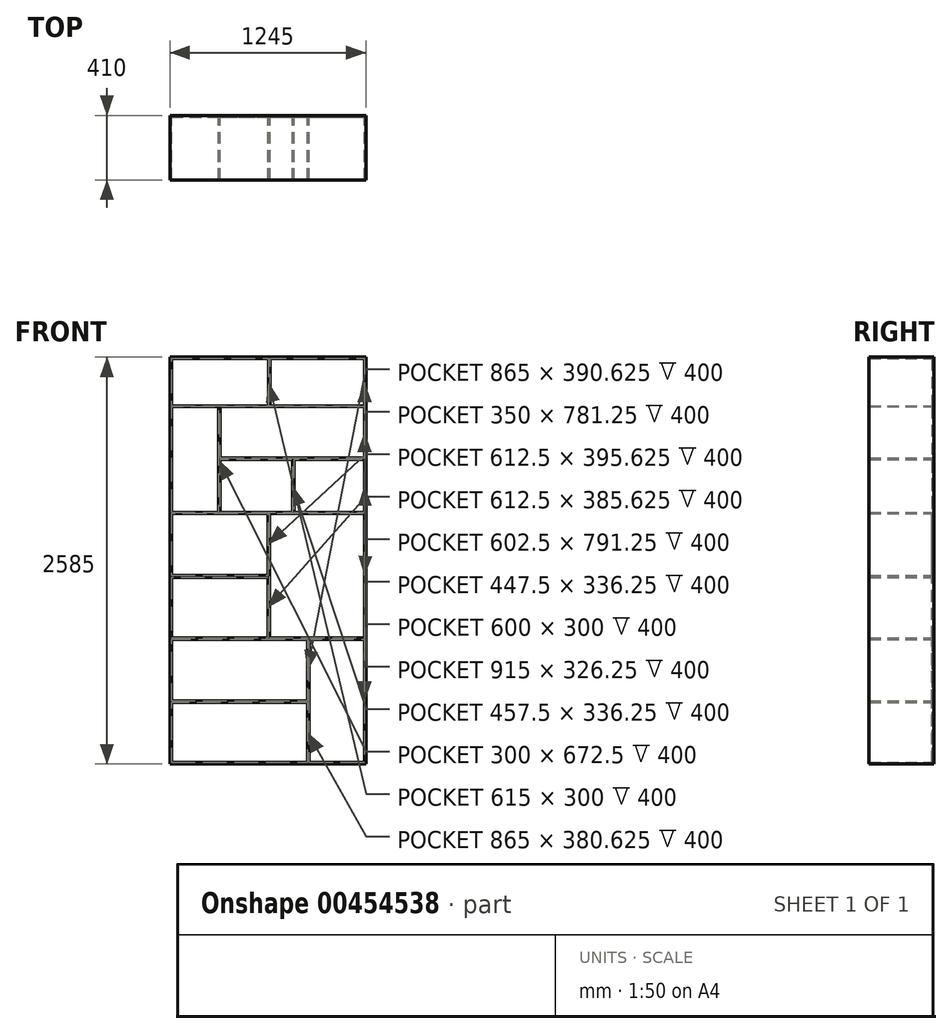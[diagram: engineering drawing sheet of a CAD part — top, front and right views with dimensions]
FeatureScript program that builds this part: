
annotation { "Feature Type Name" : "Feature", "Feature Type Description" : "" }
export const myFeature = defineFeature(function(context is Context, id is Id, definition is map)
    precondition{}
    {
        {
            var Q0;
            Q0=qCreatedBy(makeId("Front.planeOp"),FACE);
            var sketch = newSketch(context, id + "F0", { "sketchPlane" : qUnion([Q0])});
            skLineSegment(sketch, "E0.bottom", {"start": v(0, 0) * mm, "end": v(1245, 0) * mm});
            skLineSegment(sketch, "E0.top", {"start": v(0, 2585) * mm, "end": v(1245, 2585) * mm});
            skLineSegment(sketch, "E0.left", {"start": v(0, 0) * mm, "end": v(0, 2585) * mm});
            skLineSegment(sketch, "E0.right", {"start": v(1245, 0) * mm, "end": v(1245, 2585) * mm});
            skSolve(sketch);
        }
        {
            var Q0;
            Q0 = qSketchRegion(id + "F0", true);
            extrude(context, id + "F1", {"entities" : qUnion([Q0]), "depth" : 410 * mm});
        }
        {
            var Q0;
            Q0=makeQuery(id+"F1.opExtrude","CAP_FACE",FACE,{"disambiguationData":[OSD([sQuery(id+"F0.wireOp",EDGE,"E0.bottom"),sQuery(id+"F0.wireOp",EDGE,"E0.top"),sQuery(id+"F0.wireOp",EDGE,"E0.left"),sQuery(id+"F0.wireOp",EDGE,"E0.right")])],"isStart":false});
            shell(context, id + "F2", {"entities" : qUnion([Q0]), "thickness" : 10 * mm});
        }
        {
            var Q0;
            Q0=makeQuery(id+"F2.opShell","OFFSET_FACE",FACE,{"disambiguationData":[OSD([sQuery(id+"F0.wireOp",EDGE,"E0.bottom"),sQuery(id+"F0.wireOp",EDGE,"E0.top"),sQuery(id+"F0.wireOp",EDGE,"E0.left"),sQuery(id+"F0.wireOp",EDGE,"E0.right")])]});
            var sketch = newSketch(context, id + "F3", { "sketchPlane" : qUnion([Q0])});
            skLineSegment(sketch, "E1", {"start": v(622.5, 2575) * mm, "end": v(622.5, 10) * mm, "construction": true});
            skLineSegment(sketch, "E2", {"start": v(10, 1292.5) * mm, "end": v(1235, 1292.5) * mm, "construction": true});
            skLineSegment(sketch, "E3", {"start": v(1235, 1292.5) * mm, "end": v(1235, 1592.5) * mm, "construction": true});
            skLineSegment(sketch, "E4", {"start": v(1235, 1592.5) * mm, "end": v(10, 1592.5) * mm, "construction": true});
            skLineSegment(sketch, "E5", {"start": v(10, 992.5) * mm, "end": v(1235, 992.5) * mm, "construction": true});
            skLineSegment(sketch, "E6", {"start": v(10, 2270) * mm, "end": v(1235, 2270) * mm, "construction": true});
            skLineSegment(sketch, "E7", {"start": v(10, 610) * mm, "end": v(1235, 610) * mm, "construction": true});
            skLineSegment(sketch, "E8.bottom", {"start": v(10, 2270) * mm, "end": v(1235, 2270) * mm});
            skLineSegment(sketch, "E8.top", {"start": v(10, 2275) * mm, "end": v(1235, 2275) * mm});
            skLineSegment(sketch, "E8.left", {"start": v(10, 2270) * mm, "end": v(10, 2275) * mm});
            skLineSegment(sketch, "E8.right", {"start": v(1235, 2270) * mm, "end": v(1235, 2275) * mm});
            skLineSegment(sketch, "E9", {"start": v(10, 1592.5) * mm, "end": v(1235, 1592.5) * mm, "construction": true});
            skLineSegment(sketch, "E10.bottom", {"start": v(10, 1592.5) * mm, "end": v(1235, 1592.5) * mm});
            skLineSegment(sketch, "E10.top", {"start": v(10, 1597.5) * mm, "end": v(1235, 1597.5) * mm});
            skLineSegment(sketch, "E10.left", {"start": v(10, 1592.5) * mm, "end": v(10, 1597.5) * mm});
            skLineSegment(sketch, "E10.right", {"start": v(1235, 1592.5) * mm, "end": v(1235, 1597.5) * mm});
            skSolve(sketch);
        }
        {
            var Q0;
            Q0 = qSketchRegion(id + "F3", true);
            extrude(context, id + "F4", {"entities" : qUnion([Q0]), "operationType" : NewBodyOperationType.ADD, "depth" : 400 * mm});
        }
        {
            var Q0;
            {var subQ0=sQuery(id+"F0.wireOp",EDGE,"E0.left");var subQ1=sQuery(id+"F0.wireOp",EDGE,"E0.right");Q0=makeQuery(id+"F4.boolean.opBoolean","SPLIT",FACE,{"disambiguationData":[TD([makeQuery(id+"F4.opExtrude","SWEPT_FACE",FACE,{"disambiguationData":[OSD([sQuery(id+"F3.wireOp",EDGE,"E8.bottom")])]})])],"derivedFrom":makeQuery(id+"F2.opShell","OFFSET_FACE",FACE,{"disambiguationData":[OSD([sQuery(id+"F0.wireOp",EDGE,"E0.bottom"),sQuery(id+"F0.wireOp",EDGE,"E0.top"),subQ0,subQ1])]})});}
            var sketch = newSketch(context, id + "F5", { "sketchPlane" : qUnion([Q0])});
            skLineSegment(sketch, "E11.bottom", {"start": v(310, 2270) * mm, "end": v(320, 2270) * mm});
            skLineSegment(sketch, "E11.top", {"start": v(310, 1597.5) * mm, "end": v(320, 1597.5) * mm});
            skLineSegment(sketch, "E11.left", {"start": v(310, 2270) * mm, "end": v(310, 1597.5) * mm});
            skLineSegment(sketch, "E11.right", {"start": v(320, 2270) * mm, "end": v(320, 1597.5) * mm});
            skSolve(sketch);
        }
        {
            var Q0;
            Q0 = qSketchRegion(id + "F5", true);
            extrude(context, id + "F6", {"entities" : qUnion([Q0]), "operationType" : NewBodyOperationType.ADD, "depth" : 400 * mm});
        }
        {
            var Q0;
            {var subQ0=sQuery(id+"F0.wireOp",EDGE,"E0.right");var subQ1=makeQuery(id+"F2.opShell","OFFSET_FACE",FACE,{"disambiguationData":[OSD([subQ0])]});var subQ2=makeQuery(id+"F4.opExtrude","SWEPT_FACE",FACE,{"disambiguationData":[OSD([sQuery(id+"F3.wireOp",EDGE,"E8.bottom")])]});var subQ4=sQuery(id+"F0.wireOp",EDGE,"E0.left");Q0=makeQuery(id+"F6.boolean.opBoolean","SPLIT",FACE,{"disambiguationData":[TD([subQ1])],"derivedFrom":makeQuery(id+"F4.boolean.opBoolean","SPLIT",FACE,{"disambiguationData":[TD([subQ2])],"derivedFrom":makeQuery(id+"F2.opShell","OFFSET_FACE",FACE,{"disambiguationData":[OSD([sQuery(id+"F0.wireOp",EDGE,"E0.bottom"),sQuery(id+"F0.wireOp",EDGE,"E0.top"),subQ4,subQ0])]})})});}
            var sketch = newSketch(context, id + "F7", { "sketchPlane" : qUnion([Q0])});
            skLineSegment(sketch, "E12.bottom", {"start": v(320, 1943.75) * mm, "end": v(1235, 1943.75) * mm});
            skLineSegment(sketch, "E12.top", {"start": v(320, 1933.75) * mm, "end": v(1235, 1933.75) * mm});
            skLineSegment(sketch, "E12.left", {"start": v(320, 1943.75) * mm, "end": v(320, 1933.75) * mm});
            skLineSegment(sketch, "E12.right", {"start": v(1235, 1943.75) * mm, "end": v(1235, 1933.75) * mm});
            skSolve(sketch);
        }
        {
            var Q0;
            Q0 = qSketchRegion(id + "F7", true);
            extrude(context, id + "F8", {"entities" : qUnion([Q0]), "operationType" : NewBodyOperationType.ADD, "depth" : 400 * mm});
        }
        {
            var Q0;
            {var subQ0=sQuery(id+"F0.wireOp",EDGE,"E0.top");var subQ1=sQuery(id+"F0.wireOp",EDGE,"E0.left");var subQ2=sQuery(id+"F0.wireOp",EDGE,"E0.right");Q0=makeQuery(id+"F4.boolean.opBoolean","SPLIT",FACE,{"disambiguationData":[TD([makeQuery(id+"F2.opShell","OFFSET_FACE",FACE,{"disambiguationData":[OSD([subQ0])]})])],"derivedFrom":makeQuery(id+"F2.opShell","OFFSET_FACE",FACE,{"disambiguationData":[OSD([sQuery(id+"F0.wireOp",EDGE,"E0.bottom"),subQ0,subQ1,subQ2])]})});}
            var sketch = newSketch(context, id + "F9", { "sketchPlane" : qUnion([Q0])});
            skLineSegment(sketch, "E13.bottom", {"start": v(625, 2575) * mm, "end": v(635, 2575) * mm});
            skLineSegment(sketch, "E13.top", {"start": v(625, 2275) * mm, "end": v(635, 2275) * mm});
            skLineSegment(sketch, "E13.left", {"start": v(625, 2575) * mm, "end": v(625, 2275) * mm});
            skLineSegment(sketch, "E13.right", {"start": v(635, 2575) * mm, "end": v(635, 2275) * mm});
            skSolve(sketch);
        }
        {
            var Q0;
            Q0 = qSketchRegion(id + "F9", true);
            extrude(context, id + "F10", {"entities" : qUnion([Q0]), "operationType" : NewBodyOperationType.ADD, "depth" : 400 * mm});
        }
        {
            var Q0;
            {var subQ0=sQuery(id+"F0.wireOp",EDGE,"E0.right");var subQ1=makeQuery(id+"F2.opShell","OFFSET_FACE",FACE,{"disambiguationData":[OSD([subQ0])]});var subQ2=makeQuery(id+"F4.opExtrude","SWEPT_FACE",FACE,{"disambiguationData":[OSD([sQuery(id+"F3.wireOp",EDGE,"E10.top")])]});var subQ4=makeQuery(id+"F4.opExtrude","SWEPT_FACE",FACE,{"disambiguationData":[OSD([sQuery(id+"F3.wireOp",EDGE,"E8.bottom")])]});var subQ5=sQuery(id+"F0.wireOp",EDGE,"E0.left");Q0=makeQuery(id+"F8.boolean.opBoolean","SPLIT",FACE,{"disambiguationData":[TD([subQ2])],"derivedFrom":makeQuery(id+"F6.boolean.opBoolean","SPLIT",FACE,{"disambiguationData":[TD([subQ1])],"derivedFrom":makeQuery(id+"F4.boolean.opBoolean","SPLIT",FACE,{"disambiguationData":[TD([subQ4])],"derivedFrom":makeQuery(id+"F2.opShell","OFFSET_FACE",FACE,{"disambiguationData":[OSD([sQuery(id+"F0.wireOp",EDGE,"E0.bottom"),sQuery(id+"F0.wireOp",EDGE,"E0.top"),subQ5,subQ0])]})})})});}
            var sketch = newSketch(context, id + "F11", { "sketchPlane" : qUnion([Q0])});
            skLineSegment(sketch, "E14.bottom", {"start": v(777.5, 1933.75) * mm, "end": v(787.5, 1933.75) * mm});
            skLineSegment(sketch, "E14.top", {"start": v(777.5, 1597.5) * mm, "end": v(787.5, 1597.5) * mm});
            skLineSegment(sketch, "E14.left", {"start": v(777.5, 1933.75) * mm, "end": v(777.5, 1597.5) * mm});
            skLineSegment(sketch, "E14.right", {"start": v(787.5, 1933.75) * mm, "end": v(787.5, 1597.5) * mm});
            skSolve(sketch);
        }
        {
            var Q0;
            Q0 = qSketchRegion(id + "F11", true);
            extrude(context, id + "F12", {"entities" : qUnion([Q0]), "operationType" : NewBodyOperationType.ADD, "depth" : 400 * mm});
        }
        {
            var Q0;
            {var subQ0=sQuery(id+"F0.wireOp",EDGE,"E0.bottom");var subQ1=sQuery(id+"F0.wireOp",EDGE,"E0.left");var subQ2=sQuery(id+"F0.wireOp",EDGE,"E0.right");Q0=makeQuery(id+"F4.boolean.opBoolean","SPLIT",FACE,{"disambiguationData":[TD([makeQuery(id+"F2.opShell","OFFSET_FACE",FACE,{"disambiguationData":[OSD([subQ0])]})])],"derivedFrom":makeQuery(id+"F2.opShell","OFFSET_FACE",FACE,{"disambiguationData":[OSD([subQ0,sQuery(id+"F0.wireOp",EDGE,"E0.top"),subQ1,subQ2])]})});}
            var sketch = newSketch(context, id + "F13", { "sketchPlane" : qUnion([Q0])});
            skLineSegment(sketch, "E15.bottom", {"start": v(10, 801.25) * mm, "end": v(1235, 801.25) * mm});
            skLineSegment(sketch, "E15.top", {"start": v(10, 791.25) * mm, "end": v(1235, 791.25) * mm});
            skLineSegment(sketch, "E15.left", {"start": v(10, 801.25) * mm, "end": v(10, 791.25) * mm});
            skLineSegment(sketch, "E15.right", {"start": v(1235, 801.25) * mm, "end": v(1235, 791.25) * mm});
            skSolve(sketch);
        }
        {
            var Q0;
            Q0 = qSketchRegion(id + "F13", true);
            extrude(context, id + "F14", {"entities" : qUnion([Q0]), "operationType" : NewBodyOperationType.ADD, "depth" : 400 * mm});
        }
        {
            var Q0;
            {var subQ0=sQuery(id+"F0.wireOp",EDGE,"E0.left");var subQ2=sQuery(id+"F0.wireOp",EDGE,"E0.right");var subQ4=makeQuery(id+"F4.opExtrude","SWEPT_FACE",FACE,{"disambiguationData":[OSD([sQuery(id+"F3.wireOp",EDGE,"E10.bottom")])]});var subQ5=sQuery(id+"F0.wireOp",EDGE,"E0.bottom");Q0=makeQuery(id+"F14.boolean.opBoolean","SPLIT",FACE,{"disambiguationData":[TD([subQ4])],"derivedFrom":makeQuery(id+"F4.boolean.opBoolean","SPLIT",FACE,{"disambiguationData":[TD([makeQuery(id+"F2.opShell","OFFSET_FACE",FACE,{"disambiguationData":[OSD([subQ5])]})])],"derivedFrom":makeQuery(id+"F2.opShell","OFFSET_FACE",FACE,{"disambiguationData":[OSD([subQ5,sQuery(id+"F0.wireOp",EDGE,"E0.top"),subQ0,subQ2])]})})});}
            var sketch = newSketch(context, id + "F15", { "sketchPlane" : qUnion([Q0])});
            skLineSegment(sketch, "E16.bottom", {"start": v(622.5, 801.25) * mm, "end": v(632.5, 801.25) * mm});
            skLineSegment(sketch, "E16.top", {"start": v(622.5, 1592.5) * mm, "end": v(632.5, 1592.5) * mm});
            skLineSegment(sketch, "E16.left", {"start": v(622.5, 801.25) * mm, "end": v(622.5, 1592.5) * mm});
            skLineSegment(sketch, "E16.right", {"start": v(632.5, 801.25) * mm, "end": v(632.5, 1592.5) * mm});
            skSolve(sketch);
        }
        {
            var Q0;
            Q0 = qSketchRegion(id + "F15", true);
            extrude(context, id + "F16", {"entities" : qUnion([Q0]), "operationType" : NewBodyOperationType.ADD, "depth" : 400 * mm});
        }
        {
            var Q0;
            {var subQ0=sQuery(id+"F0.wireOp",EDGE,"E0.left");var subQ1=makeQuery(id+"F2.opShell","OFFSET_FACE",FACE,{"disambiguationData":[OSD([subQ0])]});var subQ3=makeQuery(id+"F4.opExtrude","SWEPT_FACE",FACE,{"disambiguationData":[OSD([sQuery(id+"F3.wireOp",EDGE,"E10.bottom")])]});var subQ4=sQuery(id+"F0.wireOp",EDGE,"E0.right");var subQ6=sQuery(id+"F0.wireOp",EDGE,"E0.bottom");Q0=makeQuery(id+"F16.boolean.opBoolean","SPLIT",FACE,{"disambiguationData":[TD([subQ1])],"derivedFrom":makeQuery(id+"F14.boolean.opBoolean","SPLIT",FACE,{"disambiguationData":[TD([subQ3])],"derivedFrom":makeQuery(id+"F4.boolean.opBoolean","SPLIT",FACE,{"disambiguationData":[TD([makeQuery(id+"F2.opShell","OFFSET_FACE",FACE,{"disambiguationData":[OSD([subQ6])]})])],"derivedFrom":makeQuery(id+"F2.opShell","OFFSET_FACE",FACE,{"disambiguationData":[OSD([subQ6,sQuery(id+"F0.wireOp",EDGE,"E0.top"),subQ0,subQ4])]})})})});}
            var sketch = newSketch(context, id + "F17", { "sketchPlane" : qUnion([Q0])});
            skLineSegment(sketch, "E17.bottom", {"start": v(10, 1196.88) * mm, "end": v(622.5, 1196.88) * mm});
            skLineSegment(sketch, "E17.top", {"start": v(10, 1186.88) * mm, "end": v(622.5, 1186.88) * mm});
            skLineSegment(sketch, "E17.left", {"start": v(10, 1196.88) * mm, "end": v(10, 1186.88) * mm});
            skLineSegment(sketch, "E17.right", {"start": v(622.5, 1196.88) * mm, "end": v(622.5, 1186.88) * mm});
            skSolve(sketch);
        }
        {
            var Q0;
            Q0 = qSketchRegion(id + "F17", true);
            extrude(context, id + "F18", {"entities" : qUnion([Q0]), "operationType" : NewBodyOperationType.ADD, "depth" : 400 * mm});
        }
        {
            var Q0;
            {var subQ0=sQuery(id+"F0.wireOp",EDGE,"E0.bottom");var subQ1=makeQuery(id+"F2.opShell","OFFSET_FACE",FACE,{"disambiguationData":[OSD([subQ0])]});var subQ2=sQuery(id+"F0.wireOp",EDGE,"E0.left");var subQ4=sQuery(id+"F0.wireOp",EDGE,"E0.right");Q0=makeQuery(id+"F14.boolean.opBoolean","SPLIT",FACE,{"disambiguationData":[TD([subQ1])],"derivedFrom":makeQuery(id+"F4.boolean.opBoolean","SPLIT",FACE,{"disambiguationData":[TD([subQ1])],"derivedFrom":makeQuery(id+"F2.opShell","OFFSET_FACE",FACE,{"disambiguationData":[OSD([subQ0,sQuery(id+"F0.wireOp",EDGE,"E0.top"),subQ2,subQ4])]})})});}
            var sketch = newSketch(context, id + "F19", { "sketchPlane" : qUnion([Q0])});
            skLineSegment(sketch, "E18.bottom", {"start": v(885, 791.25) * mm, "end": v(875, 791.25) * mm});
            skLineSegment(sketch, "E18.top", {"start": v(885, 10) * mm, "end": v(875, 10) * mm});
            skLineSegment(sketch, "E18.left", {"start": v(885, 791.25) * mm, "end": v(885, 10) * mm});
            skLineSegment(sketch, "E18.right", {"start": v(875, 791.25) * mm, "end": v(875, 10) * mm});
            skSolve(sketch);
        }
        {
            var Q0;
            Q0 = qSketchRegion(id + "F19", true);
            extrude(context, id + "F20", {"entities" : qUnion([Q0]), "operationType" : NewBodyOperationType.ADD, "depth" : 400 * mm});
        }
        {
            var Q0;
            {var subQ0=sQuery(id+"F0.wireOp",EDGE,"E0.bottom");var subQ1=makeQuery(id+"F2.opShell","OFFSET_FACE",FACE,{"disambiguationData":[OSD([subQ0])]});var subQ2=sQuery(id+"F0.wireOp",EDGE,"E0.left");var subQ3=makeQuery(id+"F2.opShell","OFFSET_FACE",FACE,{"disambiguationData":[OSD([subQ2])]});var subQ5=sQuery(id+"F0.wireOp",EDGE,"E0.right");Q0=makeQuery(id+"F20.boolean.opBoolean","SPLIT",FACE,{"disambiguationData":[TD([subQ3])],"derivedFrom":makeQuery(id+"F14.boolean.opBoolean","SPLIT",FACE,{"disambiguationData":[TD([subQ1])],"derivedFrom":makeQuery(id+"F4.boolean.opBoolean","SPLIT",FACE,{"disambiguationData":[TD([subQ1])],"derivedFrom":makeQuery(id+"F2.opShell","OFFSET_FACE",FACE,{"disambiguationData":[OSD([subQ0,sQuery(id+"F0.wireOp",EDGE,"E0.top"),subQ2,subQ5])]})})})});}
            var sketch = newSketch(context, id + "F21", { "sketchPlane" : qUnion([Q0])});
            skLineSegment(sketch, "E19.bottom", {"start": v(10, 400.63) * mm, "end": v(875, 400.63) * mm});
            skLineSegment(sketch, "E19.top", {"start": v(10, 390.62) * mm, "end": v(875, 390.62) * mm});
            skLineSegment(sketch, "E19.left", {"start": v(10, 400.63) * mm, "end": v(10, 390.62) * mm});
            skLineSegment(sketch, "E19.right", {"start": v(875, 400.63) * mm, "end": v(875, 390.62) * mm});
            skSolve(sketch);
        }
        {
            var Q0;
            Q0 = qSketchRegion(id + "F21", true);
            extrude(context, id + "F22", {"entities" : qUnion([Q0]), "operationType" : NewBodyOperationType.ADD, "depth" : 400 * mm});
        }
    });
